# Revit family: Maxlogic dedektör sıva üstü montaj kutulu
name_source: partatom
category: Fire Alarm Devices
units: mm (PartAtom-declared; Revit-internal decimal feet)

## family parameters
Cut with Voids When Loaded = No
Host = Face
Maintain Annotation Orientation = Yes
OmniClass Number = 23.85.30.21
OmniClass Title = Environmental Detection/Registration
Part Type = Normal
Room Calculation Point = No
Round Connector Dimension = Use Diameter
Shared = No

## types (10) — shared parameters
Color = Beyaz
Compatible sockets = ML-0140
Compatible sockets 2 = ML-0141
Fax Number = (+)90 216 466 45 10
Installation Manual = https://mavilielektronik.com
Main Material = White Plastic PC/ABS
Manufacturer = Mavili Elektronik Ticaret A.Ş.
Model = Maxlogic
Mounting surface = Tavana montaj
Nominal Depth = 51 mm
Nominal Height = 106 mm
Nominal Width = 106 mm
Operating temperature = (-10°C) - (+50°C)
Operatonal Voltage (default) = 26 V/DC
Recessed mounting base = ML-0150
Secondary Material = Plastic
URL = https://www.mavili.com.tr
Warranty Duration Labor = 2
Warranty Duration Parts = 2
Warranty Duration Unit = Year
Weatherproof surface mounting back box = ML-0121
zero-valued in all types: Cost, Default Elevation

## per-type parameters (varying)
| type | Algılama yarı çapı | Code Performance | Description | Device Adress Setup | Indicator output | Isı halka | Multi sensör halka | Operating voltage range | Product Code | Public Works Pose Number | Weight |
| Maxlogic Konvansiyonel Optik Duman Dedektörü, sıva üstü montaj kutulu | 6,2 m | EN 54-7 | Konvansiyonel Optik Duman Dedektörü, sıva üstü montaj kutulu |  | MG-4000 | No | No | 10-30V/DC | ML-2110 | 832-106 | 140 gr |
| Maxlogic Akıllı Adresli Optik Duman Dedektörü sıva üstü montaj kutulu | 6,2 m | EN 54-7 | Akıllı Adresli Optik Duman Dedektörü sıva üstü montaj kutulu | El tipi adresleme cihazı | MG-4000.A | No | No | 18-33V/DC | ML-1110 | 833-500 | 100 gr |
| Maxlogic Akıllı Adresli Optik Duman Dedektörü , Kısa Devre İzolatörlü sıva üstü montaj kutulu | 6,2 m | EN 54-7 / EN 54-17 | Akıllı Adresli Optik Duman Dedektörü , Kısa Devre İzolatörlü sıva üstü montaj kutulu | El tipi adresleme cihazı | MG-4000.A | No | No | 18-33V/DC | ML-1110.SCI | 833-501 | 100 gr |
| Maxlogic Konvansiyonel Sabit Sıcaklık Dedektörü sıva üstü montaj kutulu | 4,5 m | EN 54-5 | Konvansiyonel Sabit Sıcaklık Dedektörü sıva üstü montaj kutulu |  | MG-4000 | Yes | No | 10-30V/DC | ML-2120 | 832-102 | 135 gr |
| Konvansiyonel  Kombine Sıcaklık Dedektörü sıva üstü montaj kutulu | 4,5 m | EN 54-5 | Konvansiyonel  Kombine Sıcaklık Dedektörü sıva üstü montaj kutulu |  | MG-4000 | Yes | No | 10-30V/DC | ML-2130 | 832-103 | 135 gr |
| Maxlogic Akıllı Adresli Sıcaklık Dedektörü sıva üstü montaj kutulu | 4,5 m | EN 54-5 | Akıllı Adresli Sıcaklık Dedektörü sıva üstü montaj kutulu | El tipi adresleme cihazı | MG-4000.A | Yes | No | 18-33V/DC | ML-1130 | 833-520 | 95 gr |
| Maxlogic Akıllı Adresli Sıcaklık Dedektörü , Kısadevre İzolatörlü sıva üstü montaj kutulu | 4,5 m | EN 54-5 / EN 54-17 | Akıllı Adresli Sıcaklık Dedektörü sıva üstü montaj kutulu | El tipi adresleme cihazı | MG-4000.A | Yes | No | 18-33V/DC | ML-1130.SCI | 833-521 | 95 gr |
| Konvansiyonel Multisensör (Optik Duman+Sıcaklık) Dedektörü sıva üstü montaj kutulu | 4,5 m | EN 54-5 / EN 54-7 | Konvansiyonel Multisensör (Optik Duman+Sıcaklık) Dedektörü sıva üstü montaj kutulu |  | MG-4000 | Yes | Yes | 10-30V/DC | ML-2140 | 832-109 | 141 gr |
| Maxlogic Akıllı Adresli Multisensör (Optik Duman+Sıcaklık)  Dedektörü sıva üstü montaj kutulu | 4,5 m | EN 54-5 / EN 54-7 / EN 54-17 | Akıllı Adresli Multisensör (Optik Duman+Sıcaklık)  Dedektörü sıva üstü montaj kutulu | El tipi adresleme cihazı | MG-4000.A | Yes | Yes | 18-33V/DC | ML-1140 | 833-530 | 100 gr |
| Maxlogic Akıllı Adresli Multisensör(Optik Duman+Sıcaklık)  Dedektörü , Kısadevre İzolatörlü sıva üstü montaj kutulu | 4,5 m | EN 54-5 / EN 54-7 / EN 54-17 | Akıllı Adresli Multisensör(Optik Duman+Sıcaklık)  Dedektörü , Kısadevre İzolatörlü sıva üstü montaj kutulu | El tipi adresleme cihazı | MG-4000.A | Yes | Yes | 18-33V/DC | ML-1140.SCI | 833-531 | 100 gr |

## geometry (parser evidence)
native form markers: Sweep x1
no freeform markers — native parametric forms only
